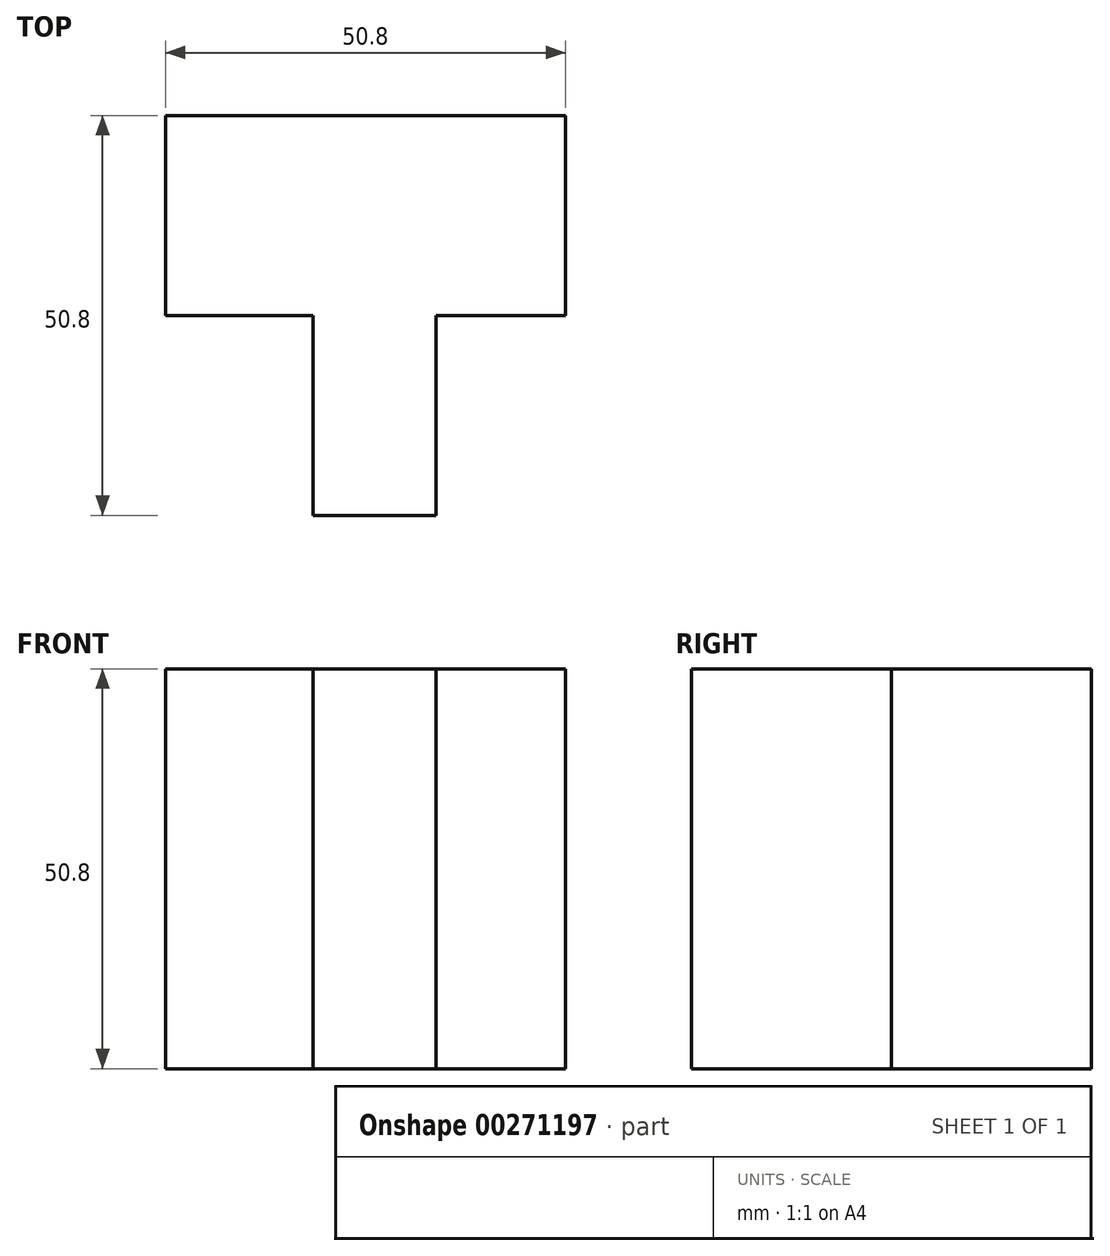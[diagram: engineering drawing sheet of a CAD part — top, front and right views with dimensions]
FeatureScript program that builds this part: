
annotation { "Feature Type Name" : "Feature", "Feature Type Description" : "" }
export const myFeature = defineFeature(function(context is Context, id is Id, definition is map)
    precondition{}
    {
        {
            var Q0;
            Q0=qCreatedBy(makeId("Front.planeOp"),FACE);
            var sketch = newSketch(context, id + "F0", { "sketchPlane" : qUnion([Q0])});
            skLineSegment(sketch, "E0.bottom", {"start": v(14.52, 0) * mm, "end": v(-36.28, 0) * mm});
            skLineSegment(sketch, "E0.top", {"start": v(14.52, 50.8) * mm, "end": v(-36.28, 50.8) * mm});
            skLineSegment(sketch, "E0.left", {"start": v(14.52, 0) * mm, "end": v(14.52, 50.8) * mm});
            skLineSegment(sketch, "E0.right", {"start": v(-36.28, 0) * mm, "end": v(-36.28, 50.8) * mm});
            skSolve(sketch);
        }
        {
            var Q0;
            Q0=makeQuery(id+"F0.imprint","IMPRINT",FACE,{"disambiguationData":[TD([[makeQuery(id+"F0.imprint","IMPRINT",EDGE,{"derivedFrom":sQuery(id+"F0.wireOp",EDGE,"E0.bottom")}),-1.0]])]});
            extrude(context, id + "F1", {"entities" : qUnion([Q0]), "depth" : 25.4 * mm});
        }
        {
            var Q0;
            Q0=makeQuery(id+"F1.opExtrude","CAP_FACE",FACE,{"disambiguationData":[OSD([sQuery(id+"F0.wireOp",EDGE,"E0.bottom"),sQuery(id+"F0.wireOp",EDGE,"E0.top"),sQuery(id+"F0.wireOp",EDGE,"E0.left"),sQuery(id+"F0.wireOp",EDGE,"E0.right")])],"isStart":false});
            var sketch = newSketch(context, id + "F2", { "sketchPlane" : qUnion([Q0])});
            skLineSegment(sketch, "E1", {"start": v(-17.57, 50.8) * mm, "end": v(-17.57, 0) * mm});
            skLineSegment(sketch, "E2", {"start": v(-1.9, 50.8) * mm, "end": v(-1.9, 0) * mm});
            skLineSegment(sketch, "E3", {"start": v(-17.57, 0) * mm, "end": v(-1.9, 0) * mm});
            skLineSegment(sketch, "E4", {"start": v(-17.57, 50.8) * mm, "end": v(-1.9, 50.8) * mm});
            skSolve(sketch);
        }
        {
            var Q0;
            Q0 = qSketchRegion(id + "F2", true);
            extrude(context, id + "F3", {"entities" : qUnion([Q0]), "operationType" : NewBodyOperationType.ADD, "depth" : 25.4 * mm});
        }
    });
